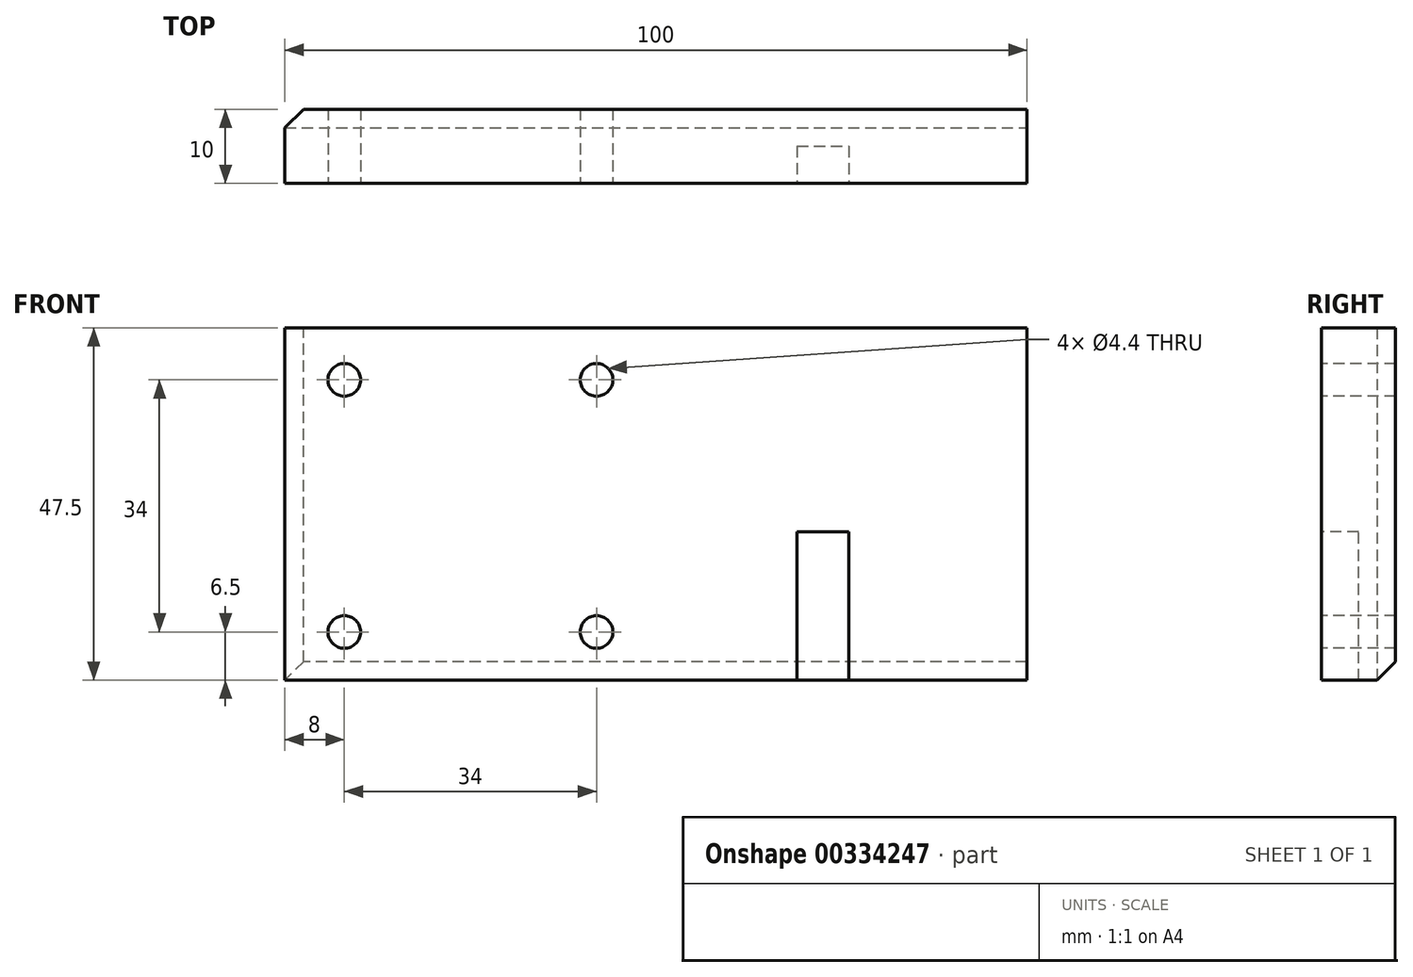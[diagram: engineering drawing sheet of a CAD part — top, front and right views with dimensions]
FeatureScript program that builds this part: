
annotation { "Feature Type Name" : "Feature", "Feature Type Description" : "" }
export const myFeature = defineFeature(function(context is Context, id is Id, definition is map)
    precondition{}
    {
        {
            var Q0;
            Q0=qCreatedBy(makeId("Front.planeOp"),FACE);
            var sketch = newSketch(context, id + "F0", { "sketchPlane" : qUnion([Q0])});
            skLineSegment(sketch, "E0.bottom", {"start": v(0, 45) * mm, "end": v(100, 45) * mm});
            skLineSegment(sketch, "E0.top", {"start": v(0, -2.5) * mm, "end": v(100, -2.5) * mm});
            skLineSegment(sketch, "E0.left", {"start": v(0, 45) * mm, "end": v(0, -2.5) * mm});
            skLineSegment(sketch, "E0.right", {"start": v(100, 45) * mm, "end": v(100, -2.5) * mm});
            skPoint(sketch, "E0.middle", {"position": v(0, 0) * mm});
            skSolve(sketch);
        }
        {
            var Q0;
            Q0 = qSketchRegion(id + "F0", true);
            extrude(context, id + "F1", {"entities" : qUnion([Q0]), "depth" : 10 * mm});
        }
        {
            var Q0;
            Q0=makeQuery(id+"F1.opExtrude","CAP_FACE",FACE,{"disambiguationData":[OSD([sQuery(id+"F0.wireOp",EDGE,"E0.bottom"),sQuery(id+"F0.wireOp",EDGE,"E0.top"),sQuery(id+"F0.wireOp",EDGE,"E0.left"),sQuery(id+"F0.wireOp",EDGE,"E0.right")])],"isStart":false});
            var sketch = newSketch(context, id + "F2", { "sketchPlane" : qUnion([Q0])});
            skLineSegment(sketch, "E1.bottom", {"start": v(8, 38) * mm, "end": v(42, 38) * mm});
            skLineSegment(sketch, "E1.top", {"start": v(8, 4) * mm, "end": v(42, 4) * mm});
            skLineSegment(sketch, "E1.left", {"start": v(8, 38) * mm, "end": v(8, 4) * mm});
            skLineSegment(sketch, "E1.right", {"start": v(42, 38) * mm, "end": v(42, 4) * mm});
            skPoint(sketch, "E1.middle", {"position": v(25, 21) * mm});
            skLineSegment(sketch, "E2.bottom", {"start": v(69, -2.5) * mm, "end": v(76, -2.5) * mm});
            skLineSegment(sketch, "E2.top", {"start": v(69, 17.5) * mm, "end": v(76, 17.5) * mm});
            skLineSegment(sketch, "E2.left", {"start": v(69, -2.5) * mm, "end": v(69, 17.5) * mm});
            skLineSegment(sketch, "E2.right", {"start": v(76, -2.5) * mm, "end": v(76, 17.5) * mm});
            skSolve(sketch);
        }
        {
            var Q0;
            Q0=sQuery(id+"F2.wireOp",VERTEX,"E1.left.start");
            var Q1;
            Q1=sQuery(id+"F2.wireOp",VERTEX,"E1.right.start");
            var Q2;
            Q2=sQuery(id+"F2.wireOp",VERTEX,"E1.top.end");
            var Q3;
            Q3=sQuery(id+"F2.wireOp",VERTEX,"E1.left.end");
            var Q4;
            Q4=makeQuery(id+"F1.opExtrude","SWEPT_BODY",BODY,{"disambiguationData":[OSD([sQuery(id+"F0.wireOp",EDGE,"E0.bottom"),sQuery(id+"F0.wireOp",EDGE,"E0.top"),sQuery(id+"F0.wireOp",EDGE,"E0.left"),sQuery(id+"F0.wireOp",EDGE,"E0.right")])]});
            hole(context, id + "F3", {"style" : HoleStyle.SIMPLE, "endStyle" : HoleEndStyle.THROUGH, "standardTappedOrClearance" : lookupTablePath({ "standard" : "ISO", "fit" : "Normal", "size" : "M4", "type" : "Clearance" }), "standardBlindInLast" : lookupTablePath({ "fit" : "Standard", "standard" : "ISO", "size" : "M4", "type" : "Clearance" }), "holeDiameter" : 4.4 * mm, "tappedDepth" : 3.75 * mm, "tapClearance" : 3, "locations" : qUnion([Q0, Q1, Q2, Q3]), "scope" : qUnion([Q4])});
        }
        {
            var Q0;
            Q0=makeQuery(id+"F2.imprint","IMPRINT",FACE,{"disambiguationData":[TD([[makeQuery(id+"F2.imprint","IMPRINT",EDGE,{"derivedFrom":sQuery(id+"F2.wireOp",EDGE,"E2.bottom")}),1.0]])]});
            extrude(context, id + "F4", {"entities" : qUnion([Q0]), "operationType" : NewBodyOperationType.REMOVE, "oppositeDirection" : true, "depth" : 5 * mm, "offsetDistance" : 25 * mm});
        }
        {
            var Q0;
            Q0=makeQuery(id+"F1.opExtrude","CAP_EDGE",EDGE,{"disambiguationData":[OSD([sQuery(id+"F0.wireOp",EDGE,"E0.left")])],"isStart":true});
            var Q1;
            Q1=makeQuery(id+"F1.opExtrude","CAP_EDGE",EDGE,{"disambiguationData":[OSD([sQuery(id+"F0.wireOp",EDGE,"E0.top")])],"isStart":true});
            chamfer(context, id + "F5", {"entities" : qUnion([Q0, Q1]), "width" : 2.5 * mm, "tangentPropagation" : true});
        }
    });
